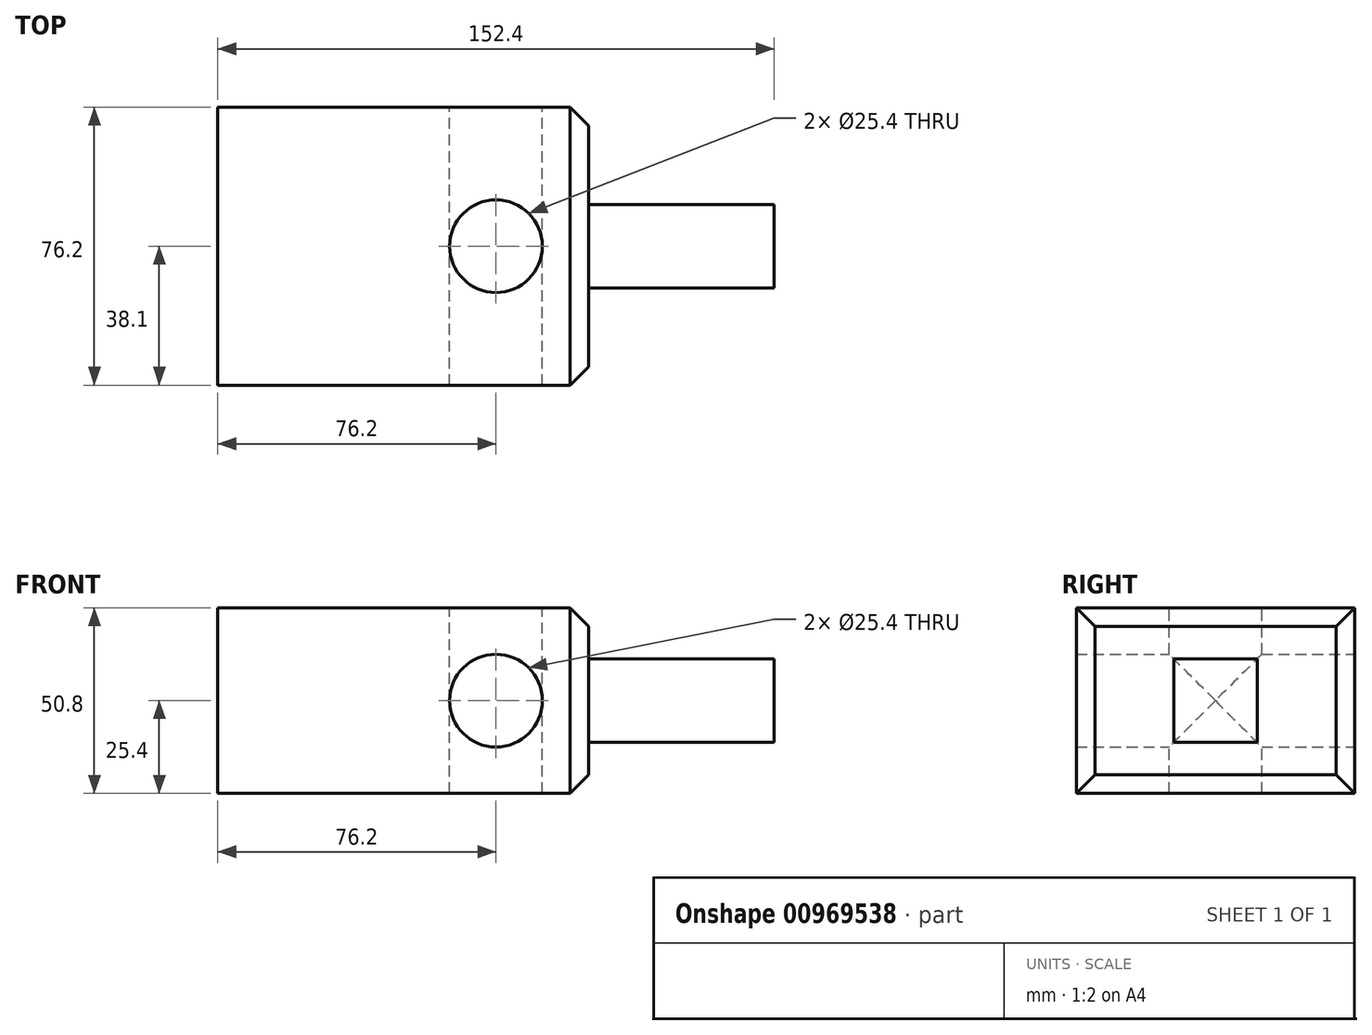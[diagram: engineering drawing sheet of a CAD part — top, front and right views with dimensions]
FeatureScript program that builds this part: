
annotation { "Feature Type Name" : "Feature", "Feature Type Description" : "" }
export const myFeature = defineFeature(function(context is Context, id is Id, definition is map)
    precondition{}
    {
        {
            var Q0;
            Q0=qCreatedBy(makeId("Top.planeOp"),FACE);
            var sketch = newSketch(context, id + "F0", { "sketchPlane" : qUnion([Q0])});
            skLineSegment(sketch, "E0.bottom", {"start": v(-50.8, 38.1) * mm, "end": v(50.8, 38.1) * mm});
            skLineSegment(sketch, "E0.top", {"start": v(-50.8, -38.1) * mm, "end": v(50.8, -38.1) * mm});
            skLineSegment(sketch, "E0.left", {"start": v(-50.8, 38.1) * mm, "end": v(-50.8, -38.1) * mm});
            skLineSegment(sketch, "E0.right", {"start": v(50.8, 38.1) * mm, "end": v(50.8, -38.1) * mm});
            skSolve(sketch);
        }
        {
            var Q0;
            Q0=makeQuery(id+"F0.imprint","IMPRINT",FACE,{"disambiguationData":[TD([[makeQuery(id+"F0.imprint","IMPRINT",EDGE,{"derivedFrom":sQuery(id+"F0.wireOp",EDGE,"E0.bottom")}),-1.0]])]});
            extrude(context, id + "F1", {"entities" : qUnion([Q0]), "depth" : 50.8 * mm, "offsetDistance" : 25.4 * mm});
        }
        {
            var Q0;
            Q0=makeQuery(id+"F1.opExtrude","SWEPT_FACE",FACE,{"disambiguationData":[OSD([sQuery(id+"F0.wireOp",EDGE,"E0.bottom")])]});
            var sketch = newSketch(context, id + "F2", { "sketchPlane" : qUnion([Q0])});
            skCircle(sketch, "E1", {"center": v(-25.4, 25.4) * mm, "radius": 12.7 * mm});
            skSolve(sketch);
        }
        {
            var Q0;
            Q0=makeQuery(id+"F1.opExtrude","CAP_FACE",FACE,{"disambiguationData":[OSD([sQuery(id+"F0.wireOp",EDGE,"E0.bottom"),sQuery(id+"F0.wireOp",EDGE,"E0.top"),sQuery(id+"F0.wireOp",EDGE,"E0.left"),sQuery(id+"F0.wireOp",EDGE,"E0.right")])],"isStart":false});
            var sketch = newSketch(context, id + "F3", { "sketchPlane" : qUnion([Q0])});
            skCircle(sketch, "E2", {"center": v(25.4, 0) * mm, "radius": 12.7 * mm});
            skSolve(sketch);
        }
        {
            var Q0;
            Q0=sQuery(id+"F2.wireOp",VERTEX,"E1.center");
            var Q1;
            Q1=makeQuery(id+"F1.opExtrude","SWEPT_BODY",BODY,{"disambiguationData":[OSD([sQuery(id+"F0.wireOp",EDGE,"E0.bottom"),sQuery(id+"F0.wireOp",EDGE,"E0.top"),sQuery(id+"F0.wireOp",EDGE,"E0.left"),sQuery(id+"F0.wireOp",EDGE,"E0.right")])]});
            hole(context, id + "F4", {"style" : HoleStyle.SIMPLE, "endStyle" : HoleEndStyle.THROUGH, "holeDiameter" : 25.4 * mm, "majorDiameter" : 6.35 * mm, "isTappedThrough" : true, "tappedDepth" : 12.7 * mm, "tapClearance" : 3, "locations" : qUnion([Q0]), "scope" : qUnion([Q1])});
        }
        {
            var Q0;
            Q0=sQuery(id+"F3.wireOp",VERTEX,"E2.center");
            var Q1;
            Q1=makeQuery(id+"F1.opExtrude","SWEPT_BODY",BODY,{"disambiguationData":[OSD([sQuery(id+"F0.wireOp",EDGE,"E0.bottom"),sQuery(id+"F0.wireOp",EDGE,"E0.top"),sQuery(id+"F0.wireOp",EDGE,"E0.left"),sQuery(id+"F0.wireOp",EDGE,"E0.right")])]});
            hole(context, id + "F5", {"style" : HoleStyle.SIMPLE, "endStyle" : HoleEndStyle.THROUGH, "holeDiameter" : 25.4 * mm, "majorDiameter" : 6.35 * mm, "isTappedThrough" : true, "tappedDepth" : 12.7 * mm, "tapClearance" : 3, "locations" : qUnion([Q0]), "scope" : qUnion([Q1])});
        }
        {
            var Q0;
            Q0=makeQuery(id+"F1.opExtrude","SWEPT_FACE",FACE,{"disambiguationData":[OSD([sQuery(id+"F0.wireOp",EDGE,"E0.right")])]});
            var sketch = newSketch(context, id + "F6", { "sketchPlane" : qUnion([Q0])});
            skLineSegment(sketch, "E3.bottom", {"start": v(-11.43, 36.83) * mm, "end": v(11.43, 36.83) * mm});
            skLineSegment(sketch, "E3.top", {"start": v(-11.43, 13.97) * mm, "end": v(11.43, 13.97) * mm});
            skLineSegment(sketch, "E3.left", {"start": v(-11.43, 36.83) * mm, "end": v(-11.43, 13.97) * mm});
            skLineSegment(sketch, "E3.right", {"start": v(11.43, 36.83) * mm, "end": v(11.43, 13.97) * mm});
            skSolve(sketch);
        }
        {
            var Q0;
            Q0 = qSketchRegion(id + "F6", true);
            extrude(context, id + "F7", {"entities" : qUnion([Q0]), "operationType" : NewBodyOperationType.ADD, "depth" : 50.8 * mm, "offsetDistance" : 25.4 * mm});
        }
        {
            var Q0;
            Q0=makeQuery(id+"F1.opExtrude","CAP_EDGE",EDGE,{"disambiguationData":[OSD([sQuery(id+"F0.wireOp",EDGE,"E0.right")])],"isStart":false});
            var Q1;
            Q1=makeQuery(id+"F1.opExtrude","SWEPT_EDGE",EDGE,{"disambiguationData":[OSD([sQuery(id+"F0.wireOp",EDGE,"E0.top"),sQuery(id+"F0.wireOp",EDGE,"E0.right")])]});
            var Q2;
            Q2=makeQuery(id+"F1.opExtrude","CAP_EDGE",EDGE,{"disambiguationData":[OSD([sQuery(id+"F0.wireOp",EDGE,"E0.right")])],"isStart":true});
            var Q3;
            Q3=makeQuery(id+"F1.opExtrude","SWEPT_EDGE",EDGE,{"disambiguationData":[OSD([sQuery(id+"F0.wireOp",EDGE,"E0.bottom"),sQuery(id+"F0.wireOp",EDGE,"E0.right")])]});
            chamfer(context, id + "F8", {"entities" : qUnion([Q0, Q1, Q2, Q3]), "width" : 5.08 * mm, "tangentPropagation" : true});
        }
    });
